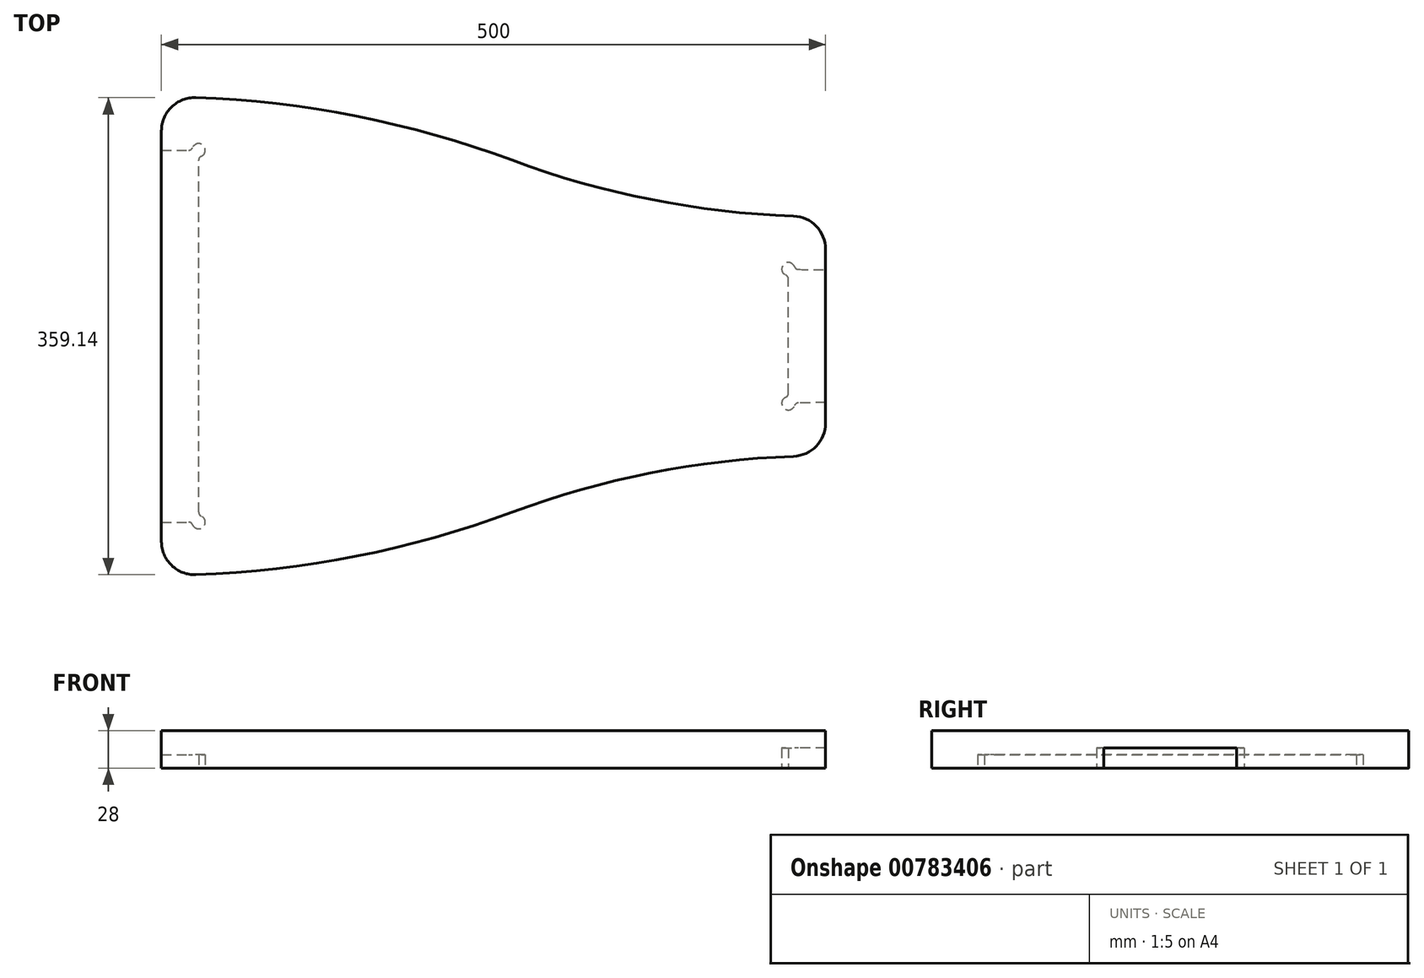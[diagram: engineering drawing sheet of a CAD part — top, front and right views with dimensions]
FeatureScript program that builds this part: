
annotation { "Feature Type Name" : "Feature", "Feature Type Description" : "" }
export const myFeature = defineFeature(function(context is Context, id is Id, definition is map)
    precondition{}
    {
        {
            var Q0;
            Q0=qCreatedBy(makeId("Top.planeOp"),FACE);
            var sketch = newSketch(context, id + "F0", { "sketchPlane" : qUnion([Q0])});
            skArc(sketch, "E0.0", {"start": v(263.95, 132.49) * mm, "mid": v(146.8, 165.63) * mm, "end": v(25.85, 179.56) * mm});
            skArc(sketch, "E1.0", {"start": v(263.95, 132.49) * mm, "mid": v(368.23, 102.95) * mm, "end": v(475.9, 90.43) * mm});
            skLineSegment(sketch, "E2", {"start": v(0, 140) * mm, "end": v(0, 154.57) * mm});
            skLineSegment(sketch, "E3", {"start": v(500, 50) * mm, "end": v(500, 65.45) * mm});
            skLineSegment(sketch, "E4", {"start": v(-157.4, 0) * mm, "end": v(716.34, 0) * mm, "construction": true});
            skPoint(sketch, "E5.visualSharp", {"position": v(0, 180) * mm});
            skArc(sketch, "E5.filletArc", {"start": v(25.85, 179.56) * mm, "mid": v(7.63, 172.55) * mm, "end": v(0, 154.57) * mm});
            skPoint(sketch, "E6.visualSharp", {"position": v(500, 90) * mm});
            skArc(sketch, "E6.filletArc", {"start": v(500, 65.45) * mm, "mid": v(492.99, 82.8) * mm, "end": v(475.9, 90.43) * mm});
            skLineSegment(sketch, "E7.0", {"start": v(28, 132.58) * mm, "end": v(28, 128.98) * mm});
            skLineSegment(sketch, "E8", {"start": v(472, 41) * mm, "end": v(472, 43.13) * mm});
            skArc(sketch, "E9.trimOffspring", {"start": v(479.43, 50.3) * mm, "mid": v(489.71, 50.07) * mm, "end": v(500, 50) * mm});
            skPoint(sketch, "E10.visualSharp", {"position": v(28, 119.44) * mm});
            skArc(sketch, "E11", {"start": v(29.88, 135.36) * mm, "mid": v(31.54, 143.54) * mm, "end": v(23.36, 141.88) * mm});
            skArc(sketch, "E12", {"start": v(476.7, 52.26) * mm, "mid": v(468.52, 54.14) * mm, "end": v(470.12, 45.91) * mm});
            skPoint(sketch, "E13.visualSharp", {"position": v(472, 45.55) * mm});
            skArc(sketch, "E13.filletArc", {"start": v(472, 43.13) * mm, "mid": v(471.49, 44.8) * mm, "end": v(470.12, 45.91) * mm});
            skPoint(sketch, "E14.visualSharp", {"position": v(477, 50.37) * mm});
            skArc(sketch, "E14.filletArc", {"start": v(476.7, 52.26) * mm, "mid": v(477.76, 50.86) * mm, "end": v(479.43, 50.3) * mm});
            skPoint(sketch, "E15.visualSharp", {"position": v(28, 135) * mm});
            skArc(sketch, "E15.filletArc", {"start": v(29.88, 135.36) * mm, "mid": v(28.51, 134.26) * mm, "end": v(28, 132.58) * mm});
            skLineSegment(sketch, "E16", {"start": v(0, 140) * mm, "end": v(20.58, 140) * mm});
            skPoint(sketch, "E17.visualSharp", {"position": v(23, 140) * mm});
            skArc(sketch, "E17.filletArc", {"start": v(20.58, 140) * mm, "mid": v(22.26, 140.51) * mm, "end": v(23.36, 141.88) * mm});
            skArc(sketch, "E18.MirrorCS", {"start": v(476.7, -52.26) * mm, "mid": v(477.76, -50.86) * mm, "end": v(479.43, -50.3) * mm});
            skArc(sketch, "E19.MirrorCS", {"start": v(472, -43.13) * mm, "mid": v(471.49, -44.8) * mm, "end": v(470.12, -45.91) * mm});
            skArc(sketch, "E20.MirrorCS", {"start": v(20.58, -140) * mm, "mid": v(22.26, -140.51) * mm, "end": v(23.36, -141.88) * mm});
            skLineSegment(sketch, "E21.MirrorCS", {"start": v(28, -132.58) * mm, "end": v(28, -128.98) * mm});
            skLineSegment(sketch, "E22.MirrorCS", {"start": v(472, -41) * mm, "end": v(472, -43.13) * mm});
            skArc(sketch, "E23.MirrorCS", {"start": v(29.88, -135.36) * mm, "mid": v(28.51, -134.26) * mm, "end": v(28, -132.58) * mm});
            skArc(sketch, "E24.MirrorCS", {"start": v(29.88, -135.36) * mm, "mid": v(31.54, -143.54) * mm, "end": v(23.36, -141.88) * mm});
            skArc(sketch, "E25.MirrorCS", {"start": v(476.7, -52.26) * mm, "mid": v(468.52, -54.14) * mm, "end": v(470.12, -45.91) * mm});
            skLineSegment(sketch, "E26.MirrorCS", {"start": v(0, -140) * mm, "end": v(20.58, -140) * mm});
            skArc(sketch, "E27.MirrorCS", {"start": v(479.43, -50.3) * mm, "mid": v(489.71, -50.07) * mm, "end": v(500, -50) * mm});
            skLineSegment(sketch, "E28.MirrorCS", {"start": v(500, -50) * mm, "end": v(500, -65.45) * mm});
            skLineSegment(sketch, "E29.MirrorCS", {"start": v(0, -140) * mm, "end": v(0, -154.57) * mm});
            skPoint(sketch, "E30.MirrorP", {"position": v(28, -135) * mm});
            skPoint(sketch, "E31.MirrorP", {"position": v(472, -45.55) * mm});
            skArc(sketch, "E32.MirrorCS", {"start": v(500, -65.45) * mm, "mid": v(492.99, -82.8) * mm, "end": v(475.9, -90.43) * mm});
            skArc(sketch, "E33.MirrorCS", {"start": v(25.85, -179.56) * mm, "mid": v(7.63, -172.55) * mm, "end": v(0, -154.57) * mm});
            skPoint(sketch, "E34.MirrorP", {"position": v(23, -140) * mm});
            skPoint(sketch, "E35.MirrorP", {"position": v(472, -30.53) * mm});
            skPoint(sketch, "E36.MirrorP", {"position": v(0, -180) * mm});
            skPoint(sketch, "E37.MirrorP", {"position": v(28, -119.44) * mm});
            skPoint(sketch, "E38.MirrorP", {"position": v(477, -50.37) * mm});
            skPoint(sketch, "E39.MirrorP", {"position": v(500, -90) * mm});
            skArc(sketch, "E40.MirrorCS", {"start": v(263.95, -132.49) * mm, "mid": v(368.23, -102.95) * mm, "end": v(475.9, -90.43) * mm});
            skArc(sketch, "E41.MirrorCS", {"start": v(263.95, -132.49) * mm, "mid": v(146.8, -165.63) * mm, "end": v(25.85, -179.56) * mm});
            skLineSegment(sketch, "E42", {"start": v(28, 128.98) * mm, "end": v(28, -128.98) * mm});
            skLineSegment(sketch, "E43", {"start": v(472, 41) * mm, "end": v(472, -41) * mm});
            skLineSegment(sketch, "E44", {"start": v(500, 50) * mm, "end": v(500, -50) * mm});
            skLineSegment(sketch, "E45", {"start": v(0, 140) * mm, "end": v(0, -140) * mm});
            skSolve(sketch);
        }
        {
            var Q0;
            Q0=makeQuery(id+"F0.imprint","IMPRINT",FACE,{"disambiguationData":[TD([[makeQuery(id+"F0.imprint","IMPRINT",EDGE,{"derivedFrom":sQuery(id+"F0.wireOp",EDGE,"E0.0")}),1.0]])]});
            extrude(context, id + "F1", {"entities" : qUnion([Q0]), "depth" : 28 * mm, "offsetDistance" : 25 * mm});
        }
        {
            var Q0;
            Q0=makeQuery(id+"F0.imprint","IMPRINT",FACE,{"disambiguationData":[TD([[makeQuery(id+"F0.imprint","IMPRINT",EDGE,{"derivedFrom":sQuery(id+"F0.wireOp",EDGE,"E7.0")}),-1.0]])]});
            extrude(context, id + "F2", {"entities" : qUnion([Q0]), "operationType" : NewBodyOperationType.ADD, "depth" : 28 * mm, "offsetDistance" : 25 * mm, "hasSecondDirection" : true, "secondDirectionOppositeDirection" : false, "secondDirectionDepth" : 10 * mm});
        }
        {
            var Q0;
            Q0=makeQuery(id+"F0.imprint","IMPRINT",FACE,{"disambiguationData":[TD([[makeQuery(id+"F0.imprint","IMPRINT",EDGE,{"derivedFrom":sQuery(id+"F0.wireOp",EDGE,"E8")}),-1.0]])]});
            extrude(context, id + "F3", {"entities" : qUnion([Q0]), "operationType" : NewBodyOperationType.ADD, "depth" : 28 * mm, "offsetDistance" : 25 * mm, "hasSecondDirection" : true, "secondDirectionOppositeDirection" : false, "secondDirectionDepth" : 15 * mm});
        }
    });
